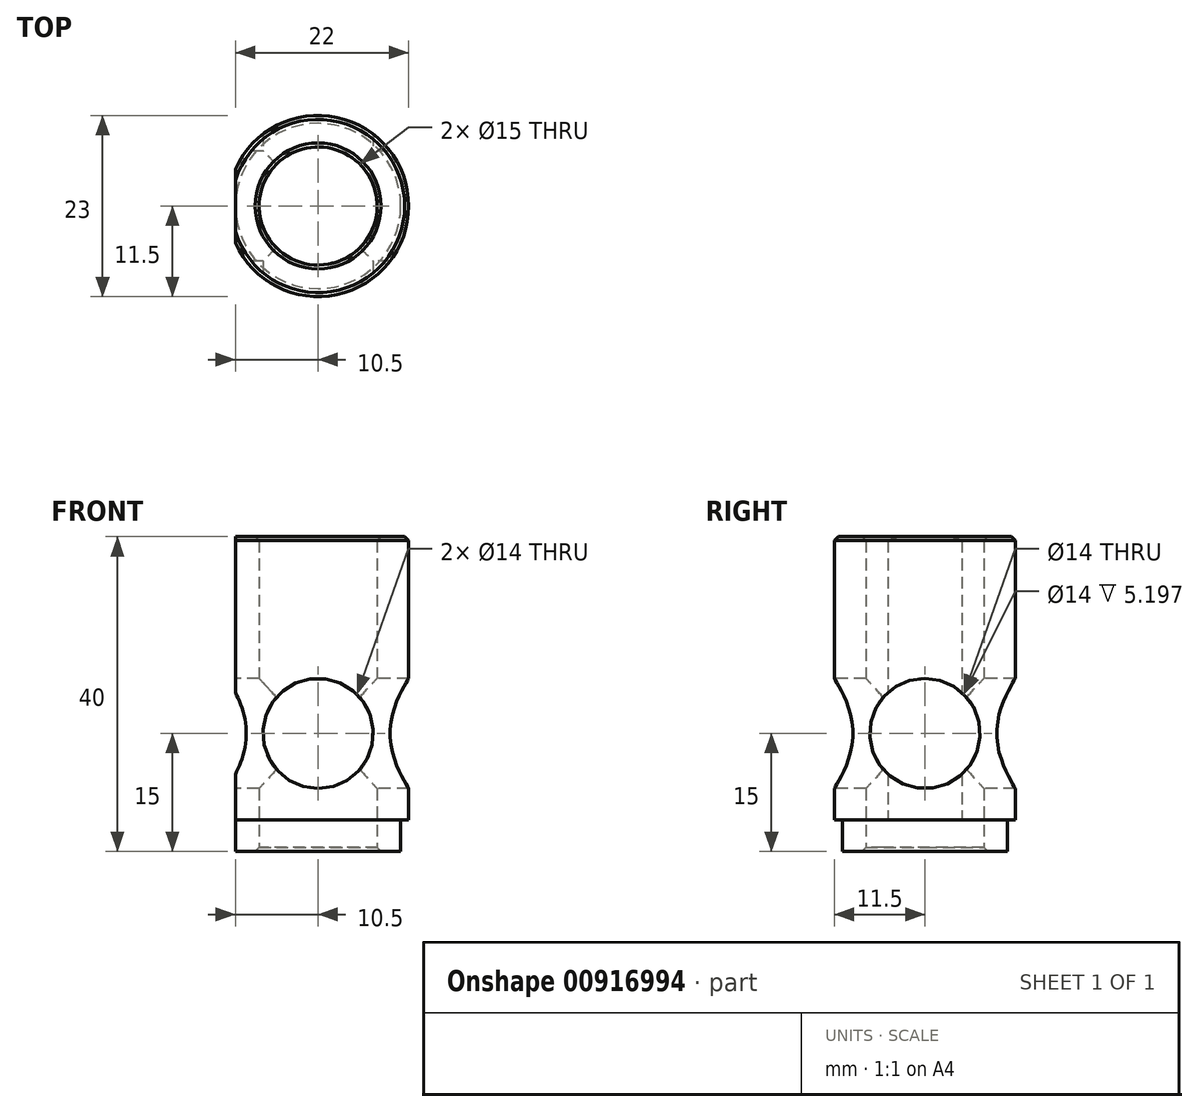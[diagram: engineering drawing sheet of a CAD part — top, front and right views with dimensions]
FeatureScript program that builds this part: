
annotation { "Feature Type Name" : "Feature", "Feature Type Description" : "" }
export const myFeature = defineFeature(function(context is Context, id is Id, definition is map)
    precondition{}
    {
        {
            var Q0;
            Q0=qCreatedBy(makeId("Top.planeOp"),FACE);
            var sketch = newSketch(context, id + "F0", { "sketchPlane" : qUnion([Q0])});
            skArc(sketch, "E0", {"start": v(-10.5, -4.7) * mm, "mid": v(11.5, 0) * mm, "end": v(-10.5, 4.7) * mm});
            skCircle(sketch, "E1", {"center": v(0, 0) * mm, "radius": 7.5 * mm});
            skLineSegment(sketch, "E2", {"start": v(0, 0) * mm, "end": v(0, -16.23) * mm, "construction": true});
            skLineSegment(sketch, "E3.0", {"start": v(-10.5, 4.7) * mm, "end": v(-10.5, -4.7) * mm});
            skSolve(sketch);
        }
        {
            var Q0;
            Q0=makeQuery(id+"F0.imprint","IMPRINT",FACE,{"disambiguationData":[TD([[makeQuery(id+"F0.imprint","IMPRINT",EDGE,{"derivedFrom":sQuery(id+"F0.wireOp",EDGE,"E0")}),1.0]])]});
            extrude(context, id + "F1", {"entities" : qUnion([Q0]), "depth" : 40 * mm, "offsetDistance" : 25 * mm});
        }
        {
            var Q0;
            Q0=makeQuery(id+"F1.opExtrude","SWEPT_FACE",FACE,{"disambiguationData":[OSD([sQuery(id+"F0.wireOp",EDGE,"E3.0")])]});
            var sketch = newSketch(context, id + "F2", { "sketchPlane" : qUnion([Q0])});
            skCircle(sketch, "E4", {"center": v(0, 15) * mm, "radius": 7 * mm});
            skPoint(sketch, "E4.centerSnap0", {"position": v(0, 40) * mm});
            skSolve(sketch);
        }
        {
            var Q0;
            Q0 = qSketchRegion(id + "F2", true);
            extrude(context, id + "F3", {"entities" : qUnion([Q0]), "operationType" : NewBodyOperationType.REMOVE, "endBound" : BoundingType.THROUGH_ALL, "oppositeDirection" : true, "depth" : 25 * mm, "offsetDistance" : 25 * mm});
        }
        {
            var Q0;
            Q0=qCreatedBy(makeId("Front.planeOp"),FACE);
            var sketch = newSketch(context, id + "F4", { "sketchPlane" : qUnion([Q0])});
            skCircle(sketch, "E5", {"center": v(0, 15) * mm, "radius": 7 * mm});
            skSolve(sketch);
        }
        {
            var Q0;
            Q0=makeQuery(id+"F4.imprint","IMPRINT",FACE,{"disambiguationData":[TD([[makeQuery(id+"F4.imprint","IMPRINT",EDGE,{"derivedFrom":sQuery(id+"F4.wireOp",EDGE,"E5")}),1.0]])]});
            extrude(context, id + "F5", {"entities" : qUnion([Q0]), "operationType" : NewBodyOperationType.REMOVE, "endBound" : BoundingType.THROUGH_ALL, "oppositeDirection" : true, "depth" : 25 * mm, "offsetDistance" : 25 * mm, "hasSecondDirection" : true, "secondDirectionBound" : BoundingType.THROUGH_ALL, "secondDirectionOppositeDirection" : false, "secondDirectionDepth" : 25 * mm});
        }
        {
            var Q0;
            Q0=makeQuery(id+"F1.opExtrude","CAP_FACE",FACE,{"disambiguationData":[OSD([sQuery(id+"F0.wireOp",EDGE,"E0"),sQuery(id+"F0.wireOp",EDGE,"E1"),sQuery(id+"F0.wireOp",EDGE,"E3.0")])],"isStart":true});
            var sketch = newSketch(context, id + "F6", { "sketchPlane" : qUnion([Q0])});
            skCircle(sketch, "E6", {"center": v(0, 0) * mm, "radius": 10.5 * mm});
            skCircle(sketch, "E7", {"center": v(0, 0) * mm, "radius": 11.5 * mm});
            skSolve(sketch);
        }
        {
            var Q0;
            Q0 = qSketchRegion(id + "F6", true);
            extrude(context, id + "F7", {"entities" : qUnion([Q0]), "operationType" : NewBodyOperationType.REMOVE, "oppositeDirection" : true, "depth" : 4 * mm, "offsetDistance" : 25 * mm});
        }
        {
            var Q0;
            Q0=makeQuery(id+"F7.boolean.opBoolean","COPY",EDGE,{"derivedFrom":makeQuery(id+"F7.opExtrude","CAP_EDGE",EDGE,{"disambiguationData":[OSD([sQuery(id+"F6.wireOp",EDGE,"E6")])],"isStart":true})});
            var Q1;
            Q1=makeQuery(id+"F1.opExtrude","CAP_EDGE",EDGE,{"disambiguationData":[OSD([sQuery(id+"F0.wireOp",EDGE,"E1")])],"isStart":true});
            var Q2;
            Q2=makeQuery(id+"F1.opExtrude","CAP_EDGE",EDGE,{"disambiguationData":[OSD([sQuery(id+"F0.wireOp",EDGE,"E0")])],"isStart":false});
            var Q3;
            Q3=makeQuery(id+"F1.opExtrude","CAP_EDGE",EDGE,{"disambiguationData":[OSD([sQuery(id+"F0.wireOp",EDGE,"E1")])],"isStart":false});
            chamfer(context, id + "F8", {"entities" : qUnion([Q0, Q1, Q2, Q3]), "width" : .5 * mm, "tangentPropagation" : true});
        }
    });
